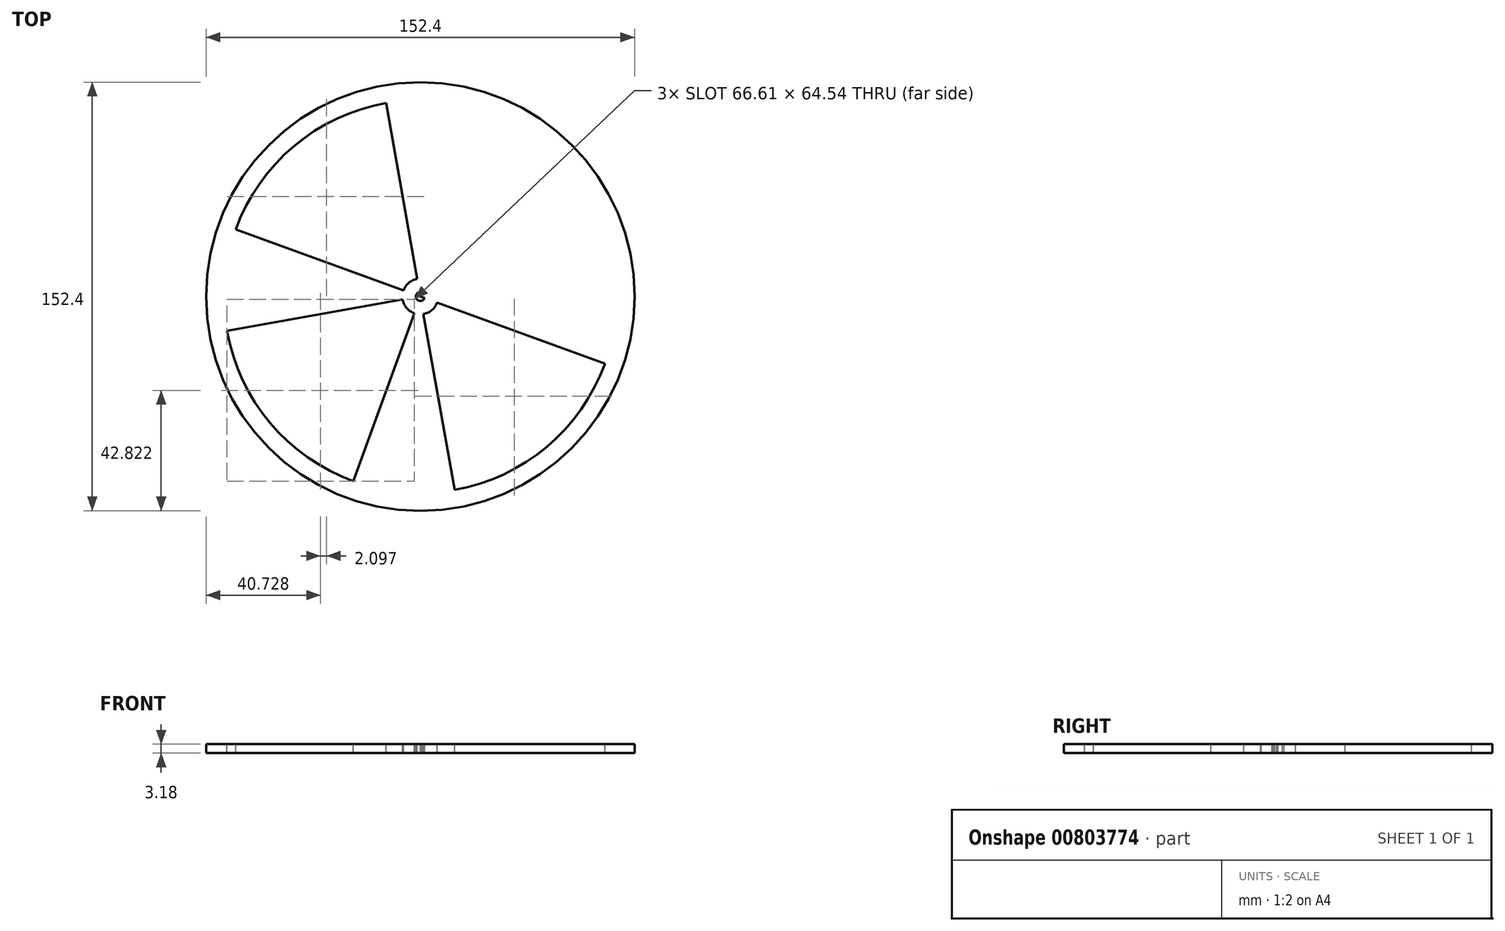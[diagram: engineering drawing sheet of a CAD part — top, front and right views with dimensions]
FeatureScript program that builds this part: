
annotation { "Feature Type Name" : "Feature", "Feature Type Description" : "" }
export const myFeature = defineFeature(function(context is Context, id is Id, definition is map)
    precondition{}
    {
        {
            var Q0;
            Q0=qCreatedBy(makeId("Top.planeOp"),FACE);
            var sketch = newSketch(context, id + "F0", { "sketchPlane" : qUnion([Q0])});
            skCircle(sketch, "E0", {"center": v(-57.7, 32.64) * mm, "radius": 76.2 * mm});
            skSolve(sketch);
        }
        {
            var Q0;
            Q0=makeQuery(id+"F0.imprint","IMPRINT",FACE,{"disambiguationData":[TD([[makeQuery(id+"F0.imprint","IMPRINT",EDGE,{"derivedFrom":sQuery(id+"F0.wireOp",EDGE,"E0")}),1.0]])]});
            extrude(context, id + "F1", {"entities" : qUnion([Q0]), "depth" : 3.17 * mm, "offsetDistance" : 25.4 * mm});
        }
        {
            var Q0;
            Q0=makeQuery(id+"F1.opExtrude","CAP_FACE",FACE,{"disambiguationData":[OSD([sQuery(id+"F0.wireOp",EDGE,"E0")])],"isStart":false});
            var sketch = newSketch(context, id + "F2", { "sketchPlane" : qUnion([Q0])});
            skCircle(sketch, "E1", {"center": v(-57.7, 32.64) * mm, "radius": 69.85 * mm});
            skLineSegment(sketch, "E2", {"start": v(-69.86, 101.42) * mm, "end": v(-57.7, 32.64) * mm});
            skLineSegment(sketch, "E3", {"start": v(-57.7, 32.64) * mm, "end": v(11.09, 44.8) * mm});
            skLineSegment(sketch, "E4", {"start": v(11.09, 44.8) * mm, "end": v(-126.48, 20.47) * mm});
            skLineSegment(sketch, "E5", {"start": v(-57.7, 32.64) * mm, "end": v(-45.53, -36.14) * mm});
            skLineSegment(sketch, "E6", {"start": v(7.95, 8.79) * mm, "end": v(-57.7, 32.64) * mm});
            skLineSegment(sketch, "E7", {"start": v(-57.7, 32.64) * mm, "end": v(-123.35, 56.5) * mm});
            skCircle(sketch, "E8", {"center": v(-57.7, 32.64) * mm, "radius": 6.35 * mm});
            skCircle(sketch, "E9", {"center": v(-57.7, 32.64) * mm, "radius": 1.59 * mm});
            skLineSegment(sketch, "E10", {"start": v(-57.7, 32.64) * mm, "end": v(-81.55, -33.01) * mm});
            skLineSegment(sketch, "E11", {"start": v(-81.55, -33.01) * mm, "end": v(-33.84, 98.3) * mm});
            skSolve(sketch);
        }
        {
            var Q0;
            {var subQ0=sQuery(id+"F2.wireOp",EDGE,"E4");var subQ1=sQuery(id+"F2.wireOp",EDGE,"E1");var subQ2=makeQuery(id+"F2.imprint","INTERSECT",VERTEX,{"disambiguationData":[OD(1.0)],"derivedFrom":[subQ1,subQ0]});Q0=makeQuery(id+"F2.imprint","IMPRINT",FACE,{"disambiguationData":[TD([[makeQuery(id+"F2.imprint","IMPRINT",EDGE,{"disambiguationData":[TD([[subQ2,-1.0]])],"derivedFrom":subQ1}),1.0]])]});}
            var Q1;
            {var subQ0=sQuery(id+"F2.wireOp",EDGE,"E2");var subQ1=sQuery(id+"F2.wireOp",EDGE,"E1");var subQ2=makeQuery(id+"F2.imprint","INTERSECT",VERTEX,{"derivedFrom":[subQ1,subQ0]});Q1=makeQuery(id+"F2.imprint","IMPRINT",FACE,{"disambiguationData":[TD([[makeQuery(id+"F2.imprint","IMPRINT",EDGE,{"disambiguationData":[TD([[subQ2,-1.0]])],"derivedFrom":subQ1}),1.0]])]});}
            var Q2;
            {var subQ0=sQuery(id+"F2.wireOp",EDGE,"E5");var subQ1=sQuery(id+"F2.wireOp",EDGE,"E1");var subQ2=makeQuery(id+"F2.imprint","INTERSECT",VERTEX,{"derivedFrom":[subQ1,subQ0]});Q2=makeQuery(id+"F2.imprint","IMPRINT",FACE,{"disambiguationData":[TD([[makeQuery(id+"F2.imprint","IMPRINT",EDGE,{"disambiguationData":[TD([[subQ2,-1.0]])],"derivedFrom":subQ1}),1.0]])]});}
            var Q3;
            {var subQ0=sQuery(id+"F2.wireOp",EDGE,"E4");var subQ1=sQuery(id+"F2.wireOp",EDGE,"E1");var subQ2=makeQuery(id+"F2.imprint","INTERSECT",VERTEX,{"disambiguationData":[OD(0.0)],"derivedFrom":[subQ1,subQ0]});Q3=makeQuery(id+"F2.imprint","IMPRINT",FACE,{"disambiguationData":[TD([[makeQuery(id+"F2.imprint","IMPRINT",EDGE,{"disambiguationData":[TD([[subQ2,-1.0]])],"derivedFrom":subQ1}),1.0]])]});}
            extrude(context, id + "F3", {"entities" : qUnion([Q0, Q1, Q2, Q3]), "operationType" : NewBodyOperationType.REMOVE, "oppositeDirection" : true, "depth" : 25.4 * mm, "offsetDistance" : 25.4 * mm});
        }
        {
            var Q0;
            {var subQ1=sQuery(id+"F2.wireOp",EDGE,"E5");var subQ3=sQuery(id+"F2.wireOp",EDGE,"E9");var subQ4=makeQuery(id+"F2.imprint","INTERSECT",VERTEX,{"derivedFrom":[subQ1,subQ3]});Q0=makeQuery(id+"F2.imprint","IMPRINT",FACE,{"disambiguationData":[TD([[makeQuery(id+"F2.imprint","IMPRINT",EDGE,{"disambiguationData":[TD([[subQ4,-1.0]])],"derivedFrom":subQ3}),1.0]])]});}
            var Q1;
            {var subQ1=sQuery(id+"F2.wireOp",EDGE,"E4");var subQ3=sQuery(id+"F2.wireOp",EDGE,"E9");var subQ4=makeQuery(id+"F2.imprint","INTERSECT",VERTEX,{"disambiguationData":[OD(0.0)],"derivedFrom":[subQ1,subQ3]});Q1=makeQuery(id+"F2.imprint","IMPRINT",FACE,{"disambiguationData":[TD([[makeQuery(id+"F2.imprint","IMPRINT",EDGE,{"disambiguationData":[TD([[subQ4,1.0]])],"derivedFrom":subQ3}),1.0]])]});}
            var Q2;
            {var subQ1=sQuery(id+"F2.wireOp",EDGE,"E4");var subQ3=sQuery(id+"F2.wireOp",EDGE,"E9");var subQ4=makeQuery(id+"F2.imprint","INTERSECT",VERTEX,{"disambiguationData":[OD(0.0)],"derivedFrom":[subQ1,subQ3]});Q2=makeQuery(id+"F2.imprint","IMPRINT",FACE,{"disambiguationData":[TD([[makeQuery(id+"F2.imprint","IMPRINT",EDGE,{"disambiguationData":[TD([[subQ4,-1.0]])],"derivedFrom":subQ3}),1.0]])]});}
            var Q3;
            {var subQ1=sQuery(id+"F2.wireOp",EDGE,"E2");var subQ3=sQuery(id+"F2.wireOp",EDGE,"E9");var subQ4=makeQuery(id+"F2.imprint","INTERSECT",VERTEX,{"derivedFrom":[subQ1,subQ3]});Q3=makeQuery(id+"F2.imprint","IMPRINT",FACE,{"disambiguationData":[TD([[makeQuery(id+"F2.imprint","IMPRINT",EDGE,{"disambiguationData":[TD([[subQ4,1.0]])],"derivedFrom":subQ3}),1.0]])]});}
            var Q4;
            {var subQ1=sQuery(id+"F2.wireOp",EDGE,"E2");var subQ3=sQuery(id+"F2.wireOp",EDGE,"E9");var subQ4=makeQuery(id+"F2.imprint","INTERSECT",VERTEX,{"derivedFrom":[subQ1,subQ3]});Q4=makeQuery(id+"F2.imprint","IMPRINT",FACE,{"disambiguationData":[TD([[makeQuery(id+"F2.imprint","IMPRINT",EDGE,{"disambiguationData":[TD([[subQ4,-1.0]])],"derivedFrom":subQ3}),1.0]])]});}
            var Q5;
            {var subQ1=sQuery(id+"F2.wireOp",EDGE,"E4");var subQ3=sQuery(id+"F2.wireOp",EDGE,"E9");var subQ4=makeQuery(id+"F2.imprint","INTERSECT",VERTEX,{"disambiguationData":[OD(1.0)],"derivedFrom":[subQ1,subQ3]});Q5=makeQuery(id+"F2.imprint","IMPRINT",FACE,{"disambiguationData":[TD([[makeQuery(id+"F2.imprint","IMPRINT",EDGE,{"disambiguationData":[TD([[subQ4,1.0]])],"derivedFrom":subQ3}),1.0]])]});}
            var Q6;
            {var subQ1=sQuery(id+"F2.wireOp",EDGE,"E4");var subQ3=sQuery(id+"F2.wireOp",EDGE,"E9");var subQ4=makeQuery(id+"F2.imprint","INTERSECT",VERTEX,{"disambiguationData":[OD(1.0)],"derivedFrom":[subQ1,subQ3]});Q6=makeQuery(id+"F2.imprint","IMPRINT",FACE,{"disambiguationData":[TD([[makeQuery(id+"F2.imprint","IMPRINT",EDGE,{"disambiguationData":[TD([[subQ4,-1.0]])],"derivedFrom":subQ3}),1.0]])]});}
            var Q7;
            {var subQ1=sQuery(id+"F2.wireOp",EDGE,"E5");var subQ3=sQuery(id+"F2.wireOp",EDGE,"E9");var subQ4=makeQuery(id+"F2.imprint","INTERSECT",VERTEX,{"derivedFrom":[subQ1,subQ3]});Q7=makeQuery(id+"F2.imprint","IMPRINT",FACE,{"disambiguationData":[TD([[makeQuery(id+"F2.imprint","IMPRINT",EDGE,{"disambiguationData":[TD([[subQ4,1.0]])],"derivedFrom":subQ3}),1.0]])]});}
            extrude(context, id + "F4", {"entities" : qUnion([Q0, Q1, Q2, Q3, Q4, Q5, Q6, Q7]), "operationType" : NewBodyOperationType.REMOVE, "oppositeDirection" : true, "depth" : 25.4 * mm, "offsetDistance" : 25.4 * mm});
        }
    });
